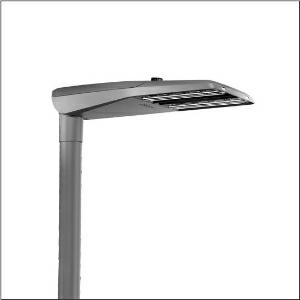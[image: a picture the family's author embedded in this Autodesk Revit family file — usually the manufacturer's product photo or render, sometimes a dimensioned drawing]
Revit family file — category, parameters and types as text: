
# Revit family: streetlight_sl_11_iq_midi___st1_2a_5xc3a51u08me_6b2b
name_source: partatom
category: Lighting Fixtures
units: mm (PartAtom-declared; Revit-internal decimal feet)

## family parameters
Cut with Voids When Loaded = No
Host = Face
Light Source = No
Part Type = Normal
Room Calculation Point = No
Round Connector Dimension = Use Diameter
Shared = No

## types (1)
- --- (1 x LED, 18110 lm, 122.7 W, 3000K)
    Apparent Load = 123 VA
    CIE Flux Codes = 32 70 96 100 100
    Color Rendering = 70
    Color Temperature = 3000K
    Default Elevation = 1800 mm
    Description = Streetlight SL 11 iQ midi, mast luminaire, primary light control with 3 zone facetted reflector, of plastic, silver coated, highly specular, primary optical cover: cover, of PMMA, transparent, light distribution: ST1.2a, light emission: direct distribution, primary light characteristic: asymmetric, installation type: post-top, side-entry, lamps: LED, High Power LED, rated values: 18.110lm | 122,7W | 147,6lm/W (begin service life); end service life: 18.110lm | 130,2W; at 50% lumin. flux: 9.055lm | 56,1W | 161,4lm/W, colour temperature: 3000K, colour rendering: CRI > 70, light colour: 730, light setting 1 begin service life: 100% | 18.110lm | 122,7W | 147,6lm/W | 3.000K, light setting 1 end service life: 130,2W, further light settings possible, control: pre-setting: logarithmic dimming characteristic, Street-Remote, Auto-Match, Temp-Guard, Lumen-Switch, Night-Set, Smart-Wire, Light-Fading, Desk-Remote (wireless, voltage-free reading and setting of iQ features in the workshop via application-optimized NFC function/RFID function), optimised constant luminous flux control (CLO 2.0), with cable H07RN-F 5x 1.5mm², mains connection: 230..240V, AC, 50/60Hz, connection cable pre-assembled, cable length: 12,5m, luminaire housing, of diecast aluminium, powder-coated, Siteco® metallic grey (DB 702S), please order mast flange separately, inclination adjustable without tools: 0°, 5°, 10°, 15° (post-top) | 0°, -5°, -10°, -15° (side-entry), sealing non-destructively replaceable, multi-level sealing system, length: 780mm, width: 376mm, height: 118mm, mast flange for spigot size: 42mm (side-entry): 5XC10008XM4, 60/48mm (side-entry/post-top): 5XC10108XM2, 76/60mm (side-entry/post-top): 5XC10108XM1, equipment: Power, Smart Interface below, protection rating (complete): IP66, insulation class (complete): insulation class II (safety insulation), certification: CE, ENEC, ENEC+, VDE, UKCA, impact resistance: IK10, permissible operating ambient temperature for outdoor applications: -25..+50°C, standard-compliant lighting for roads and squares, Environmental Product Declaration (EPD) tested and certified by an independent institute, packaging unit: 1 piece

Light Distribution: ST1.2a
    Height = 118 mm
    Lamp = 1 x LED
    Lamp Light Flux = 18110 lm
    Lamp Power = 122.7 W
    Lamp count = 1
    Length = 780 mm
    Luminous efficacy = 148 lm/W
    Manufacturer = Siteco
    ModVariant = No
    Model = 5XC3A51U08ME
    Number of Poles = 1
    OnlyDefault = Yes
    Power Factor = 1
    Product Name = Streetlight SL 11 iQ midi | ST1.2a
    Product group = mast luminaire | pylon top
    ProductGroupID = 6100
    Protection Class = Protection class II
    Protection Degree = IP 66
    RLX_Detail_Level = 1
    RLX_Emergency_Light_Flux = 0 lm
    RLX_Emergency_Type = 0
    RLX_Emergency_Type_DB = No
    RlxData = <blob elided: 70037 chars, md5=42ac6313>
    Socket = socket
    Standby Power = 0 W
    System Light Flux = 18111 lm
    System Power = 123 W
    Type Comments = factory setting: luminous flux: 100 % | dim-lin: 254 | 553 mA
    Type Image = l_1005968.jpg
    URL = http://relux.com
    VarID = @adj_133228
    Voltage = 0 V
    Weight = 0.00 kg
    Width = 376 mm

## geometry (parser evidence)
native form markers: Blend x4, Sweep x11
no freeform markers — native parametric forms only
